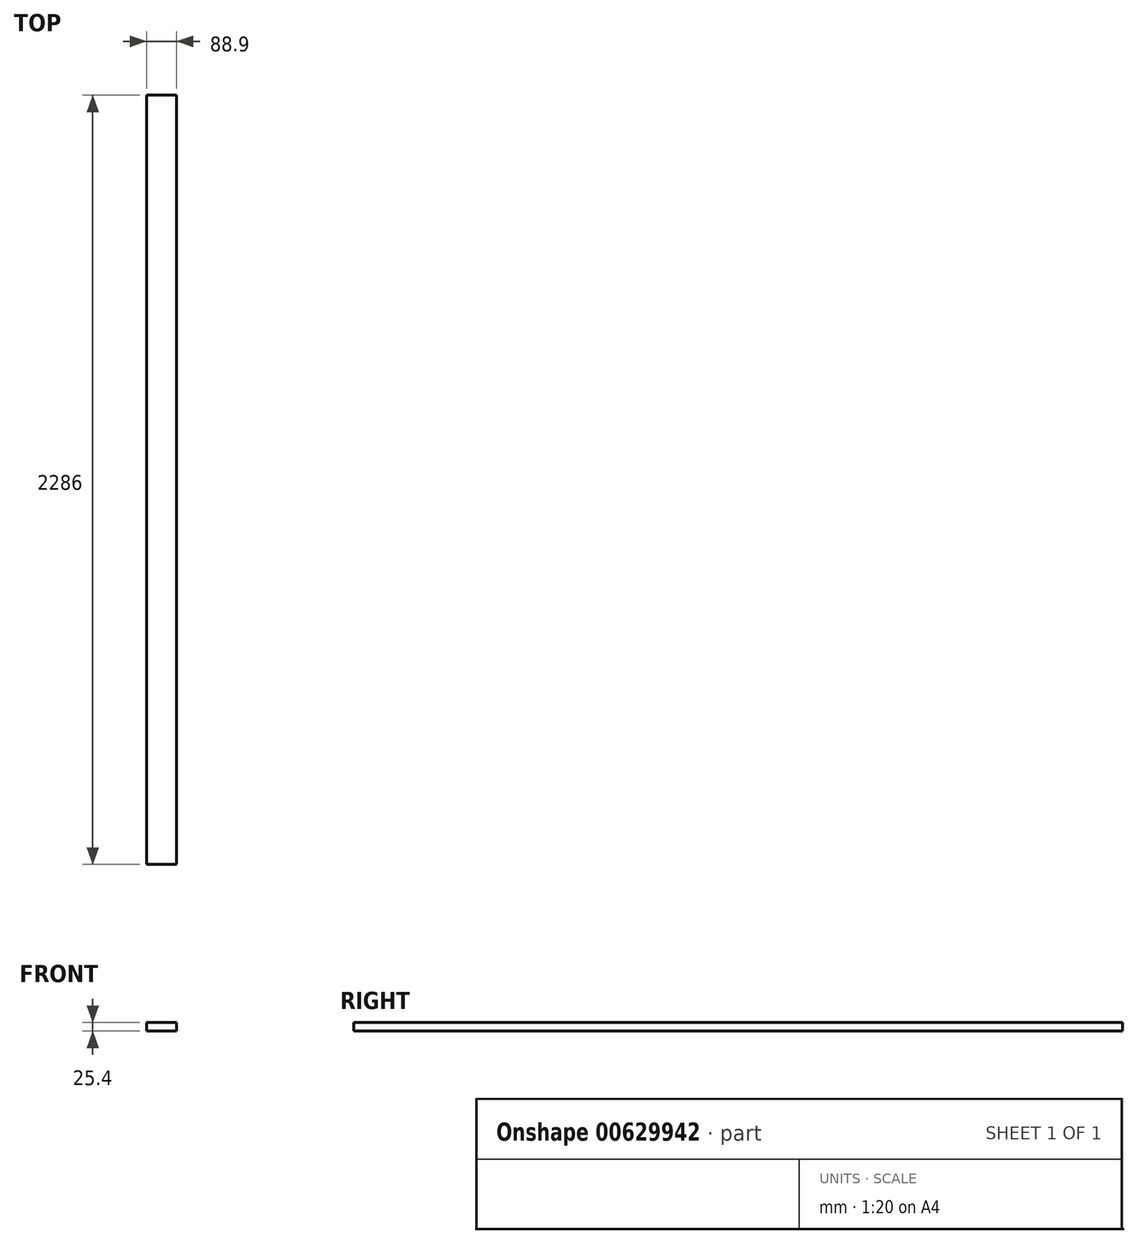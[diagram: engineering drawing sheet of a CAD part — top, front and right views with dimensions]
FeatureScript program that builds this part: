
annotation { "Feature Type Name" : "Feature", "Feature Type Description" : "" }
export const myFeature = defineFeature(function(context is Context, id is Id, definition is map)
    precondition{}
    {
        {
            var Q0;
            Q0=qCreatedBy(makeId("Front.planeOp"),FACE);
            var sketch = newSketch(context, id + "F0", { "sketchPlane" : qUnion([Q0])});
            skLineSegment(sketch, "E0.bottom", {"start": v(-14.23, 25.4) * mm, "end": v(74.67, 25.4) * mm});
            skLineSegment(sketch, "E0.top", {"start": v(-14.23, 0) * mm, "end": v(74.67, 0) * mm});
            skLineSegment(sketch, "E0.left", {"start": v(-14.23, 25.4) * mm, "end": v(-14.23, 0) * mm});
            skLineSegment(sketch, "E0.right", {"start": v(74.67, 25.4) * mm, "end": v(74.67, 0) * mm});
            skSolve(sketch);
        }
        {
            var Q0;
            Q0 = qSketchRegion(id + "F0", true);
            extrude(context, id + "F1", {"entities" : qUnion([Q0]), "depth" : 2286 * mm, "offsetDistance" : 25.4 * mm});
        }
    });
